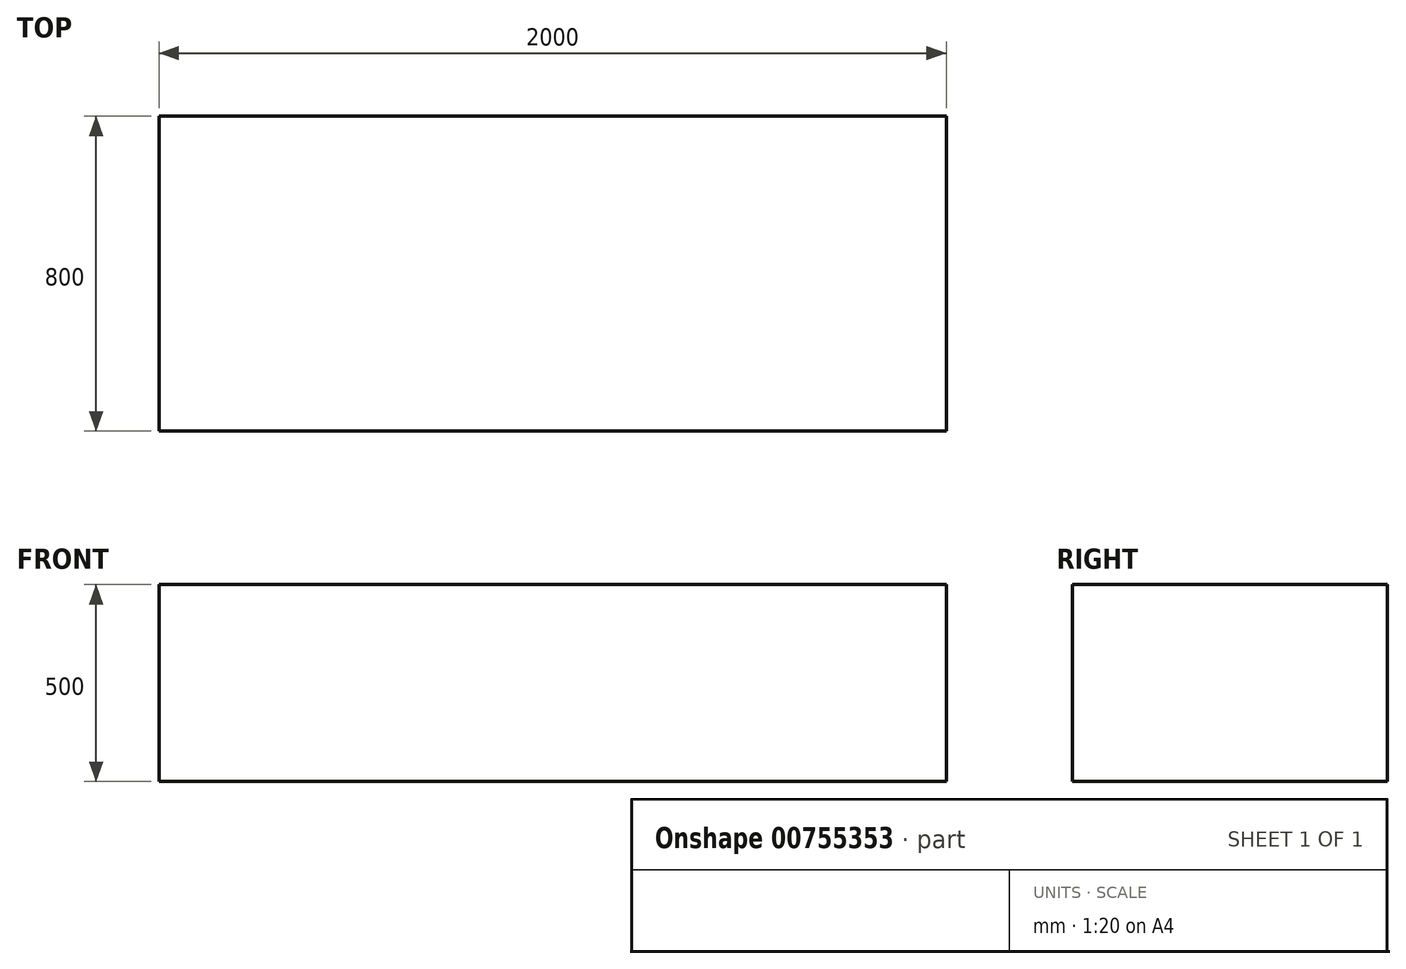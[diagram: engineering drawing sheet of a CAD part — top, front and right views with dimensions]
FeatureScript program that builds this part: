
annotation { "Feature Type Name" : "Feature", "Feature Type Description" : "" }
export const myFeature = defineFeature(function(context is Context, id is Id, definition is map)
    precondition{}
    {
        {
            var Q0;
            Q0=qCreatedBy(makeId("Top.planeOp"),FACE);
            var sketch = newSketch(context, id + "F0", { "sketchPlane" : qUnion([Q0])});
            skLineSegment(sketch, "E0.bottom", {"start": v(1000, 400) * mm, "end": v(-1000, 400) * mm});
            skLineSegment(sketch, "E0.top", {"start": v(1000, -400) * mm, "end": v(-1000, -400) * mm});
            skLineSegment(sketch, "E0.left", {"start": v(1000, 400) * mm, "end": v(1000, -400) * mm});
            skLineSegment(sketch, "E0.right", {"start": v(-1000, 400) * mm, "end": v(-1000, -400) * mm});
            skPoint(sketch, "E0.middle", {"position": v(0, 0) * mm});
            skSolve(sketch);
        }
        {
            var Q0;
            Q0 = qSketchRegion(id + "F0", true);
            extrude(context, id + "F1", {"entities" : qUnion([Q0]), "depth" : 500 * mm, "offsetDistance" : 25 * mm});
        }
    });
